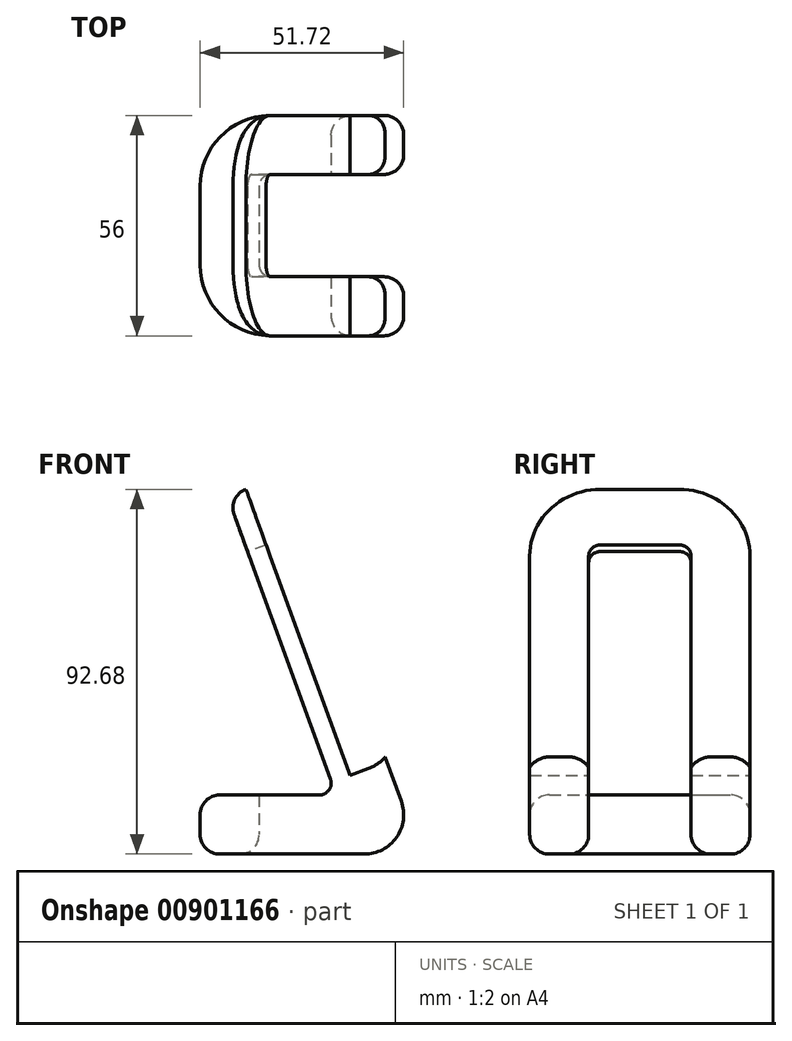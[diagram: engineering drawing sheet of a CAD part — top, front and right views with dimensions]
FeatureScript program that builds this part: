
annotation { "Feature Type Name" : "Feature", "Feature Type Description" : "" }
export const myFeature = defineFeature(function(context is Context, id is Id, definition is map)
    precondition{}
    {
        {
            var Q0;
            Q0=qCreatedBy(makeId("Front.planeOp"),FACE);
            var sketch = newSketch(context, id + "F0", { "sketchPlane" : qUnion([Q0])});
            skLineSegment(sketch, "E0", {"start": v(11.63, 92.68) * mm, "end": v(6.93, 90.97) * mm});
            skLineSegment(sketch, "E1", {"start": v(6.93, 90.97) * mm, "end": v(34.58, 15) * mm});
            skLineSegment(sketch, "E2", {"start": v(34.58, 15) * mm, "end": v(0, 15) * mm});
            skLineSegment(sketch, "E3", {"start": v(0, 15) * mm, "end": v(0, 0) * mm});
            skLineSegment(sketch, "E4", {"start": v(0, 0) * mm, "end": v(56, 0) * mm});
            skLineSegment(sketch, "E5", {"start": v(56, 0) * mm, "end": v(47.02, 24.68) * mm});
            skLineSegment(sketch, "E6", {"start": v(47.02, 24.68) * mm, "end": v(37.62, 21.26) * mm, "construction": true});
            skLineSegment(sketch, "E7", {"start": v(37.62, 21.26) * mm, "end": v(11.63, 92.68) * mm});
            skLineSegment(sketch, "E8", {"start": v(37.62, 21.26) * mm, "end": v(-17.1, 171.6) * mm, "construction": true});
            skPoint(sketch, "E9", {"position": v(92.5, 160.02) * mm});
            skLineSegment(sketch, "E10", {"start": v(10.26, 96.43) * mm, "end": v(10.26, 0) * mm, "construction": true});
            skArc(sketch, "E11", {"start": v(37.62, 21.26) * mm, "mid": v(42.78, 21.71) * mm, "end": v(47.02, 24.68) * mm});
            skLineSegment(sketch, "E12", {"start": v(37.62, 21.26) * mm, "end": v(38.08, 20) * mm});
            skLineSegment(sketch, "E13", {"start": v(38.08, 20) * mm, "end": v(42.78, 21.71) * mm});
            skSolve(sketch);
        }
        {
            var Q0;
            Q0=makeQuery(id+"F0.imprint","IMPRINT",FACE,{"disambiguationData":[TD([[makeQuery(id+"F0.imprint","IMPRINT",EDGE,{"derivedFrom":sQuery(id+"F0.wireOp",EDGE,"E0")}),1.0]])]});
            extrude(context, id + "F1", {"entities" : qUnion([Q0]), "depth" : 56 * mm, "offsetDistance" : 25 * mm});
        }
        {
            var Q0;
            Q0=makeQuery(id+"F1.opExtrude","SWEPT_FACE",FACE,{"disambiguationData":[OSD([sQuery(id+"F0.wireOp",EDGE,"E4")])]});
            var sketch = newSketch(context, id + "F2", { "sketchPlane" : qUnion([Q0])});
            skLineSegment(sketch, "E14.bottom", {"start": v(15, 41) * mm, "end": v(56, 41) * mm});
            skLineSegment(sketch, "E14.top", {"start": v(15, 15) * mm, "end": v(56, 15) * mm});
            skLineSegment(sketch, "E14.left", {"start": v(15, 41) * mm, "end": v(15, 15) * mm});
            skLineSegment(sketch, "E14.right", {"start": v(56, 41) * mm, "end": v(56, 15) * mm});
            skSolve(sketch);
        }
        {
            var Q0;
            Q0=makeQuery(id+"F2.imprint","IMPRINT",FACE,{"disambiguationData":[TD([[makeQuery(id+"F2.imprint","IMPRINT",EDGE,{"derivedFrom":sQuery(id+"F2.wireOp",EDGE,"E14.bottom")}),-1.0]])]});
            var Q1;
            Q1=makeQuery(id+"F1.opExtrude","SWEPT_FACE",FACE,{"disambiguationData":[OSD([sQuery(id+"F0.wireOp",EDGE,"E2")])]});
            extrude(context, id + "F3", {"entities" : qUnion([Q0]), "operationType" : NewBodyOperationType.REMOVE, "endBound" : BoundingType.UP_TO_SURFACE, "oppositeDirection" : true, "depth" : 25 * mm, "endBoundEntityFace" : qUnion([Q1]), "offsetDistance" : 25 * mm});
        }
        {
            var Q0;
            Q0=makeQuery(id+"F1.opExtrude","SWEPT_FACE",FACE,{"disambiguationData":[OSD([sQuery(id+"F0.wireOp",EDGE,"E1")])]});
            var sketch = newSketch(context, id + "F4", { "sketchPlane" : qUnion([Q0])});
            skLineSegment(sketch, "E15.bottom", {"start": v(15, 68.1) * mm, "end": v(41, 68.1) * mm});
            skLineSegment(sketch, "E15.top", {"start": v(15, -11.9) * mm, "end": v(41, -11.9) * mm});
            skLineSegment(sketch, "E15.left", {"start": v(15, 68.1) * mm, "end": v(15, -11.9) * mm});
            skLineSegment(sketch, "E15.right", {"start": v(41, 68.1) * mm, "end": v(41, -11.9) * mm});
            skSolve(sketch);
        }
        {
            var Q0;
            Q0=qSketchRegion(id+"F4",true);
            var Q1;
            Q1=makeQuery(id+"F1.opExtrude","SWEPT_FACE",FACE,{"disambiguationData":[OSD([sQuery(id+"F0.wireOp",EDGE,"E5")])]});
            extrude(context, id + "F5", {"entities" : qUnion([Q0]), "operationType" : NewBodyOperationType.REMOVE, "endBound" : BoundingType.UP_TO_SURFACE, "oppositeDirection" : true, "depth" : 25 * mm, "endBoundEntityFace" : qUnion([Q1]), "offsetDistance" : 25 * mm});
        }
        {
            var Q0;
            {var subQ0=sQuery(id+"F0.wireOp",EDGE,"E5");var subQ1=sQuery(id+"F0.wireOp",EDGE,"E4");Q0=makeQuery(id+"F3.boolean.opBoolean","SPLIT",EDGE,{"disambiguationData":[TD([makeQuery(id+"F3.opExtrude","SWEPT_FACE",FACE,{"disambiguationData":[OSD([sQuery(id+"F2.wireOp",EDGE,"E14.top")])]})])],"derivedFrom":makeQuery(id+"F1.opExtrude","SWEPT_EDGE",EDGE,{"disambiguationData":[OSD([subQ1,subQ0])]})});}
            var Q1;
            {var subQ0=sQuery(id+"F0.wireOp",EDGE,"E5");var subQ1=sQuery(id+"F0.wireOp",EDGE,"E4");Q1=makeQuery(id+"F3.boolean.opBoolean","SPLIT",EDGE,{"disambiguationData":[TD([makeQuery(id+"F3.opExtrude","SWEPT_FACE",FACE,{"disambiguationData":[OSD([sQuery(id+"F2.wireOp",EDGE,"E14.bottom")])]})])],"derivedFrom":makeQuery(id+"F1.opExtrude","SWEPT_EDGE",EDGE,{"disambiguationData":[OSD([subQ1,subQ0])]})});}
            fillet(context, id + "F6", {"entities" : qUnion([Q0, Q1]), "radius" : 10 * mm, "tangentPropagation" : true, "allowEdgeOverflow" : false});
        }
        {
            var Q0;
            Q0=makeQuery(id+"F1.opExtrude","CAP_EDGE",EDGE,{"disambiguationData":[OSD([sQuery(id+"F0.wireOp",EDGE,"E3")])],"isStart":false});
            var Q1;
            Q1=makeQuery(id+"F1.opExtrude","CAP_EDGE",EDGE,{"disambiguationData":[OSD([sQuery(id+"F0.wireOp",EDGE,"E3")])],"isStart":true});
            var Q2;
            Q2=makeQuery(id+"F1.opExtrude","CAP_EDGE",EDGE,{"disambiguationData":[OSD([sQuery(id+"F0.wireOp",EDGE,"E0")])],"isStart":false});
            var Q3;
            Q3=makeQuery(id+"F1.opExtrude","CAP_EDGE",EDGE,{"disambiguationData":[OSD([sQuery(id+"F0.wireOp",EDGE,"E0")])],"isStart":true});
            fillet(context, id + "F7", {"entities" : qUnion([Q0, Q1, Q2, Q3]), "radius" : 18 * mm, "tangentPropagation" : true, "allowEdgeOverflow" : false});
        }
        {
            var Q0;
            Q0=makeQuery(id+"F3.boolean.opBoolean","COPY",EDGE,{"derivedFrom":makeQuery(id+"F3.opExtrude","SWEPT_EDGE",EDGE,{"disambiguationData":[OSD([sQuery(id+"F2.wireOp",EDGE,"E14.top"),sQuery(id+"F2.wireOp",EDGE,"E14.left")])]})});
            var Q1;
            Q1=makeQuery(id+"F3.boolean.opBoolean","COPY",EDGE,{"derivedFrom":makeQuery(id+"F3.opExtrude","SWEPT_EDGE",EDGE,{"disambiguationData":[OSD([sQuery(id+"F2.wireOp",EDGE,"E14.bottom"),sQuery(id+"F2.wireOp",EDGE,"E14.left")])]})});
            var Q2;
            Q2=makeQuery(id+"F5.boolean.opBoolean","COPY",EDGE,{"derivedFrom":makeQuery(id+"F5.opExtrude","SWEPT_EDGE",EDGE,{"disambiguationData":[OSD([sQuery(id+"F4.wireOp",EDGE,"E15.bottom"),sQuery(id+"F4.wireOp",EDGE,"E15.left")])]})});
            var Q3;
            Q3=makeQuery(id+"F5.boolean.opBoolean","COPY",EDGE,{"derivedFrom":makeQuery(id+"F5.opExtrude","SWEPT_EDGE",EDGE,{"disambiguationData":[OSD([sQuery(id+"F4.wireOp",EDGE,"E15.bottom"),sQuery(id+"F4.wireOp",EDGE,"E15.right")])]})});
            var Q4;
            {var subQ0=sQuery(id+"F2.wireOp",EDGE,"E14.top");var subQ1=sQuery(id+"F0.wireOp",EDGE,"E1");var subQ2=makeQuery(id+"F1.opExtrude","SWEPT_FACE",FACE,{"disambiguationData":[OSD([subQ1])]});var subQ3=sQuery(id+"F0.wireOp",EDGE,"E2");var subQ4=makeQuery(id+"F1.opExtrude","SWEPT_FACE",FACE,{"disambiguationData":[OSD([subQ3])]});Q4=makeQuery(id+"F3.boolean.opBoolean","SPLIT",EDGE,{"disambiguationData":[topologyDisambiguationEdgeConnected([subQ2,subQ4]),TD([makeQuery(id+"F3.opExtrude","SWEPT_FACE",FACE,{"disambiguationData":[OSD([subQ0])]})])],"derivedFrom":makeQuery(id+"F1.opExtrude","SWEPT_EDGE",EDGE,{"disambiguationData":[OSD([subQ1,subQ3])]})});}
            var Q5;
            {var subQ0=sQuery(id+"F0.wireOp",EDGE,"E2");var subQ1=makeQuery(id+"F1.opExtrude","SWEPT_FACE",FACE,{"disambiguationData":[OSD([subQ0])]});var subQ2=sQuery(id+"F2.wireOp",EDGE,"E14.bottom");var subQ3=sQuery(id+"F0.wireOp",EDGE,"E1");var subQ4=makeQuery(id+"F1.opExtrude","SWEPT_FACE",FACE,{"disambiguationData":[OSD([subQ3])]});Q5=makeQuery(id+"F3.boolean.opBoolean","SPLIT",EDGE,{"disambiguationData":[topologyDisambiguationEdgeConnected([subQ4,subQ1]),TD([makeQuery(id+"F3.opExtrude","SWEPT_FACE",FACE,{"disambiguationData":[OSD([subQ2])]})])],"derivedFrom":makeQuery(id+"F1.opExtrude","SWEPT_EDGE",EDGE,{"disambiguationData":[OSD([subQ3,subQ0])]})});}
            fillet(context, id + "F8", {"entities" : qUnion([Q0, Q1, Q2, Q3, Q4, Q5]), "radius" : 3 * mm, "tangentPropagation" : true, "allowEdgeOverflow" : false});
        }
        {
            var Q0;
            Q0=makeQuery(id+"F1.opExtrude","CAP_EDGE",EDGE,{"disambiguationData":[OSD([sQuery(id+"F0.wireOp",EDGE,"E1")])],"isStart":false});
            var Q1;
            Q1=makeQuery(id+"F7.opFillet","BLEND_EDGE",EDGE,{"blendedFrom":[makeQuery(id+"F1.opExtrude","CAP_EDGE",EDGE,{"disambiguationData":[OSD([sQuery(id+"F0.wireOp",EDGE,"E3")])],"isStart":false}),makeQuery(id+"F1.opExtrude","SWEPT_FACE",FACE,{"disambiguationData":[OSD([sQuery(id+"F0.wireOp",EDGE,"E4")])]})],"blendedInto":[makeQuery(id+"F1.opExtrude","SWEPT_FACE",FACE,{"disambiguationData":[OSD([sQuery(id+"F0.wireOp",EDGE,"E4")])]})]});
            var Q2;
            {var subQ0=sQuery(id+"F2.wireOp",EDGE,"E14.top");Q2=makeQuery(id+"F3.boolean.opBoolean","COPY",EDGE,{"disambiguationData":[topologyDisambiguationEdgeConnected([makeQuery(id+"F1.opExtrude","SWEPT_FACE",FACE,{"disambiguationData":[OSD([sQuery(id+"F0.wireOp",EDGE,"E2")])]})])],"derivedFrom":makeQuery(id+"F3.opExtrude","CAP_EDGE",EDGE,{"disambiguationData":[OSD([subQ0])],"isStart":false})});}
            var Q3;
            {var subQ0=makeQuery(id+"F3.opExtrude","SWEPT_FACE",FACE,{"disambiguationData":[OSD([sQuery(id+"F2.wireOp",EDGE,"E14.top")])]});var subQ1=sQuery(id+"F0.wireOp",EDGE,"E5");var subQ2=sQuery(id+"F0.wireOp",EDGE,"E4");Q3=makeQuery(id+"F6.opFillet","BLEND_EDGE",EDGE,{"blendedFrom":[makeQuery(id+"F3.boolean.opBoolean","SPLIT",EDGE,{"disambiguationData":[TD([subQ0])],"derivedFrom":makeQuery(id+"F1.opExtrude","SWEPT_EDGE",EDGE,{"disambiguationData":[OSD([subQ2,subQ1])]})}),makeQuery(id+"F5.boolean.opBoolean","MERGE",FACE,{"derivedFrom":[makeQuery(id+"F3.boolean.opBoolean","COPY",FACE,{"derivedFrom":subQ0})],"fromTools":[makeQuery(id+"F5.opExtrude","SWEPT_FACE",FACE,{"disambiguationData":[OSD([sQuery(id+"F4.wireOp",EDGE,"E15.left")])]})]})],"blendedInto":[makeQuery(id+"F5.boolean.opBoolean","MERGE",FACE,{"derivedFrom":[makeQuery(id+"F3.boolean.opBoolean","COPY",FACE,{"derivedFrom":subQ0})],"fromTools":[makeQuery(id+"F5.opExtrude","SWEPT_FACE",FACE,{"disambiguationData":[OSD([sQuery(id+"F4.wireOp",EDGE,"E15.left")])]})]})]});}
            fillet(context, id + "F9", {"entities" : qUnion([Q0, Q1, Q2, Q3]), "radius" : 5 * mm, "tangentPropagation" : true, "allowEdgeOverflow" : false});
        }
    });
